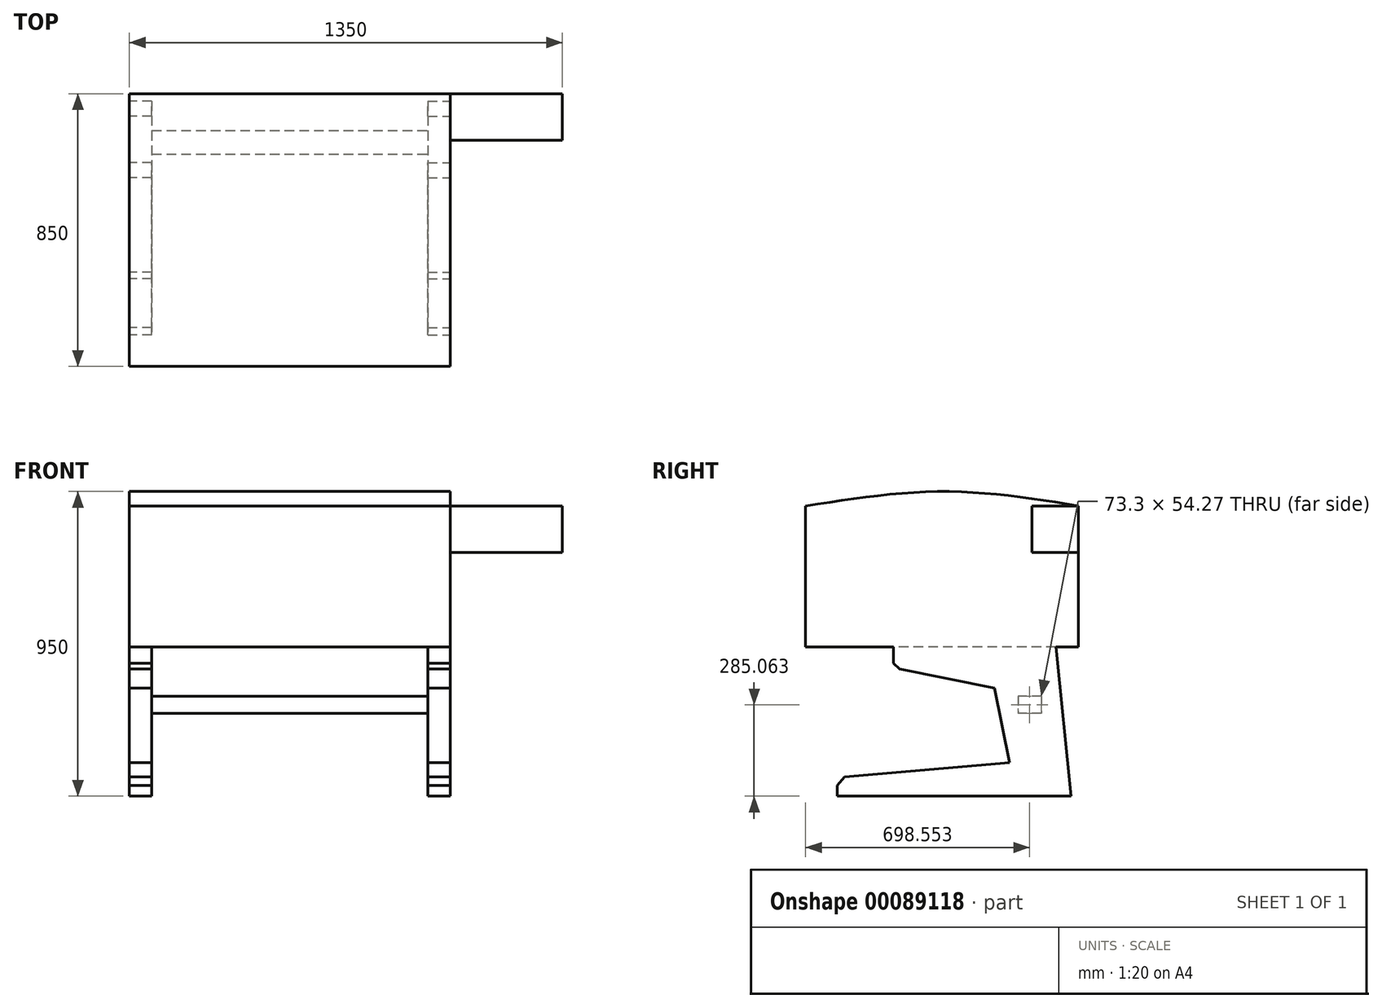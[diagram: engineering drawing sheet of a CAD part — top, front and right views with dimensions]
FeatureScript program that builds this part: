
annotation { "Feature Type Name" : "Feature", "Feature Type Description" : "" }
export const myFeature = defineFeature(function(context is Context, id is Id, definition is map)
    precondition{}
    {
        {
            var Q0;
            Q0=qCreatedBy(makeId("Right.planeOp"),FACE);
            var sketch = newSketch(context, id + "F0", { "sketchPlane" : qUnion([Q0])});
            skLineSegment(sketch, "E0.top", {"start": v(314.21, -296.81) * mm, "end": v(-535.79, -296.81) * mm});
            skLineSegment(sketch, "E0.left", {"start": v(314.21, 143.19) * mm, "end": v(314.21, -296.81) * mm});
            skLineSegment(sketch, "E0.right", {"start": v(-535.79, 143.19) * mm, "end": v(-535.79, -296.81) * mm});
            skFitSpline(sketch, "E1", {"points": [v(314.21, 143.19) * mm, v(-101.07, 188.19) * mm, v(-535.79, 143.19) * mm], "startDerivative": vector(-835.2, 138.23) * mm, "endDerivative": vector(-864.68, -137.2) * mm});
            skLineSegment(sketch, "E2", {"start": v(314.21, 143.19) * mm, "end": v(-535.79, 143.19) * mm, "construction": true});
            skSolve(sketch);
        }
        {
            var Q0;
            Q0=makeQuery(id+"F0.imprint","IMPRINT",FACE,{"disambiguationData":[TD([[makeQuery(id+"F0.imprint","IMPRINT",EDGE,{"derivedFrom":sQuery(id+"F0.wireOp",EDGE,"E0.top")}),-1.0]])]});
            extrude(context, id + "F1", {"entities" : qUnion([Q0]), "depth" : 1000 * mm});
        }
        {
            var Q0;
            Q0=makeQuery(id+"F1.opExtrude","CAP_FACE",FACE,{"disambiguationData":[OSD([sQuery(id+"F0.wireOp",EDGE,"E0.top"),sQuery(id+"F0.wireOp",EDGE,"E0.left"),sQuery(id+"F0.wireOp",EDGE,"E0.right"),sQuery(id+"F0.wireOp",EDGE,"E1")])],"isStart":false});
            var sketch = newSketch(context, id + "F2", { "sketchPlane" : qUnion([Q0])});
            skLineSegment(sketch, "E3.bottom", {"start": v(314.21, 143.19) * mm, "end": v(169.21, 143.19) * mm});
            skLineSegment(sketch, "E3.top", {"start": v(314.21, -1.81) * mm, "end": v(169.21, -1.81) * mm});
            skLineSegment(sketch, "E3.left", {"start": v(314.21, 143.19) * mm, "end": v(314.21, -1.81) * mm});
            skLineSegment(sketch, "E3.right", {"start": v(169.21, 143.19) * mm, "end": v(169.21, -1.81) * mm});
            skSolve(sketch);
        }
        {
            var Q0;
            Q0=makeQuery(id+"F2.imprint","IMPRINT",FACE,{"disambiguationData":[TD([[makeQuery(id+"F2.imprint","IMPRINT",EDGE,{"derivedFrom":sQuery(id+"F2.wireOp",EDGE,"E3.bottom")}),1.0]])]});
            extrude(context, id + "F3", {"entities" : qUnion([Q0]), "operationType" : NewBodyOperationType.ADD, "depth" : 350 * mm});
        }
        {
            var Q0;
            Q0=makeQuery(id+"F1.opExtrude","CAP_FACE",FACE,{"disambiguationData":[OSD([sQuery(id+"F0.wireOp",EDGE,"E0.top"),sQuery(id+"F0.wireOp",EDGE,"E0.left"),sQuery(id+"F0.wireOp",EDGE,"E0.right"),sQuery(id+"F0.wireOp",EDGE,"E1")])],"isStart":false});
            var sketch = newSketch(context, id + "F4", { "sketchPlane" : qUnion([Q0])});
            skLineSegment(sketch, "E4", {"start": v(244.73, -296.81) * mm, "end": v(291.2, -761.8) * mm});
            skLineSegment(sketch, "E5", {"start": v(291.2, -761.8) * mm, "end": v(-437.1, -761.8) * mm});
            skLineSegment(sketch, "E6", {"start": v(-437.1, -761.8) * mm, "end": v(-437.1, -728.36) * mm});
            skLineSegment(sketch, "E7", {"start": v(-437.1, -728.36) * mm, "end": v(-414.3, -701) * mm});
            skLineSegment(sketch, "E8", {"start": v(-414.3, -701) * mm, "end": v(99.63, -656.9) * mm});
            skLineSegment(sketch, "E9", {"start": v(99.63, -656.9) * mm, "end": v(52.5, -424.26) * mm});
            skLineSegment(sketch, "E10", {"start": v(52.5, -424.26) * mm, "end": v(-242.48, -364.97) * mm});
            skLineSegment(sketch, "E11", {"start": v(-242.48, -364.97) * mm, "end": v(-262.24, -346.72) * mm});
            skLineSegment(sketch, "E12", {"start": v(-262.24, -346.72) * mm, "end": v(-262.24, -296.81) * mm});
            skLineSegment(sketch, "E13", {"start": v(-262.24, -296.81) * mm, "end": v(244.73, -296.81) * mm});
            skLineSegment(sketch, "E14", {"start": v(-530, 188.2) * mm, "end": v(338.33, 188.2) * mm, "construction": true});
            skSolve(sketch);
        }
        {
            var Q0;
            Q0=makeQuery(id+"F4.imprint","IMPRINT",FACE,{"disambiguationData":[TD([[makeQuery(id+"F4.imprint","IMPRINT",EDGE,{"derivedFrom":sQuery(id+"F4.wireOp",EDGE,"E4")}),-1.0]])]});
            extrude(context, id + "F5", {"entities" : qUnion([Q0]), "oppositeDirection" : true, "depth" : 70 * mm});
        }
        {
            var Q0;
            Q0=makeQuery(id+"F1.opExtrude","CAP_FACE",FACE,{"disambiguationData":[OSD([sQuery(id+"F0.wireOp",EDGE,"E0.top"),sQuery(id+"F0.wireOp",EDGE,"E0.left"),sQuery(id+"F0.wireOp",EDGE,"E0.right"),sQuery(id+"F0.wireOp",EDGE,"E1")])],"isStart":true});
            var Q1;
            Q1=makeQuery(id+"F1.opExtrude","CAP_FACE",FACE,{"disambiguationData":[OSD([sQuery(id+"F0.wireOp",EDGE,"E0.top"),sQuery(id+"F0.wireOp",EDGE,"E0.left"),sQuery(id+"F0.wireOp",EDGE,"E0.right"),sQuery(id+"F0.wireOp",EDGE,"E1")])],"isStart":false});
            cPlane(context, id + "F6", {"entities" : qUnion([Q0, Q1]), "cplaneType" : CPlaneType.MID_PLANE, "offset" : 150 * mm, "width" : 150 * mm, "height" : 150 * mm});
        }
        {
            var Q0;
            Q0=makeQuery(id+"F5.opExtrude","SWEPT_BODY",BODY,{"disambiguationData":[OSD([sQuery(id+"F4.wireOp",EDGE,"E4"),sQuery(id+"F4.wireOp",EDGE,"E5"),sQuery(id+"F4.wireOp",EDGE,"E6"),sQuery(id+"F4.wireOp",EDGE,"E7"),sQuery(id+"F4.wireOp",EDGE,"E8"),sQuery(id+"F4.wireOp",EDGE,"E9"),sQuery(id+"F4.wireOp",EDGE,"E10"),sQuery(id+"F4.wireOp",EDGE,"E11"),sQuery(id+"F4.wireOp",EDGE,"E12"),sQuery(id+"F4.wireOp",EDGE,"E13")])]});
            var Q1;
            Q1=qCreatedBy(id+"F6.planeOp",FACE);
            mirror(context, id + "F7", {"operationType" : NewBodyOperationType.ADD, "entities" : qUnion([Q0]), "mirrorPlane" : qUnion([Q1])});
        }
        {
            var Q0;
            Q0=makeQuery(id+"F5.opExtrude","CAP_FACE",FACE,{"disambiguationData":[OSD([sQuery(id+"F4.wireOp",EDGE,"E4"),sQuery(id+"F4.wireOp",EDGE,"E5"),sQuery(id+"F4.wireOp",EDGE,"E6"),sQuery(id+"F4.wireOp",EDGE,"E7"),sQuery(id+"F4.wireOp",EDGE,"E8"),sQuery(id+"F4.wireOp",EDGE,"E9"),sQuery(id+"F4.wireOp",EDGE,"E10"),sQuery(id+"F4.wireOp",EDGE,"E11"),sQuery(id+"F4.wireOp",EDGE,"E12"),sQuery(id+"F4.wireOp",EDGE,"E13")])],"isStart":false});
            var sketch = newSketch(context, id + "F8", { "sketchPlane" : qUnion([Q0])});
            skLineSegment(sketch, "E15.bottom", {"start": v(-199.41, -449.61) * mm, "end": v(-126.11, -449.61) * mm});
            skLineSegment(sketch, "E15.top", {"start": v(-199.41, -503.88) * mm, "end": v(-126.11, -503.88) * mm});
            skLineSegment(sketch, "E15.left", {"start": v(-199.41, -449.61) * mm, "end": v(-199.41, -503.88) * mm});
            skLineSegment(sketch, "E15.right", {"start": v(-126.11, -449.61) * mm, "end": v(-126.11, -503.88) * mm});
            skSolve(sketch);
        }
        {
            var Q0;
            Q0=makeQuery(id+"F8.imprint","IMPRINT",FACE,{"disambiguationData":[TD([[makeQuery(id+"F8.imprint","IMPRINT",EDGE,{"derivedFrom":sQuery(id+"F8.wireOp",EDGE,"E15.bottom")}),-1.0]])]});
            var Q1;
            Q1=makeQuery(id+"F7.opPattern","COPY",FACE,{"derivedFrom":makeQuery(id+"F5.opExtrude","CAP_FACE",FACE,{"disambiguationData":[OSD([sQuery(id+"F4.wireOp",EDGE,"E4"),sQuery(id+"F4.wireOp",EDGE,"E5"),sQuery(id+"F4.wireOp",EDGE,"E6"),sQuery(id+"F4.wireOp",EDGE,"E7"),sQuery(id+"F4.wireOp",EDGE,"E8"),sQuery(id+"F4.wireOp",EDGE,"E9"),sQuery(id+"F4.wireOp",EDGE,"E10"),sQuery(id+"F4.wireOp",EDGE,"E11"),sQuery(id+"F4.wireOp",EDGE,"E12"),sQuery(id+"F4.wireOp",EDGE,"E13")])],"isStart":false}),"instanceName":"1"});
            extrude(context, id + "F9", {"entities" : qUnion([Q0]), "operationType" : NewBodyOperationType.ADD, "endBound" : BoundingType.UP_TO_SURFACE, "endBoundEntityFace" : qUnion([Q1]), "depth" : 25 * mm});
        }
    });
